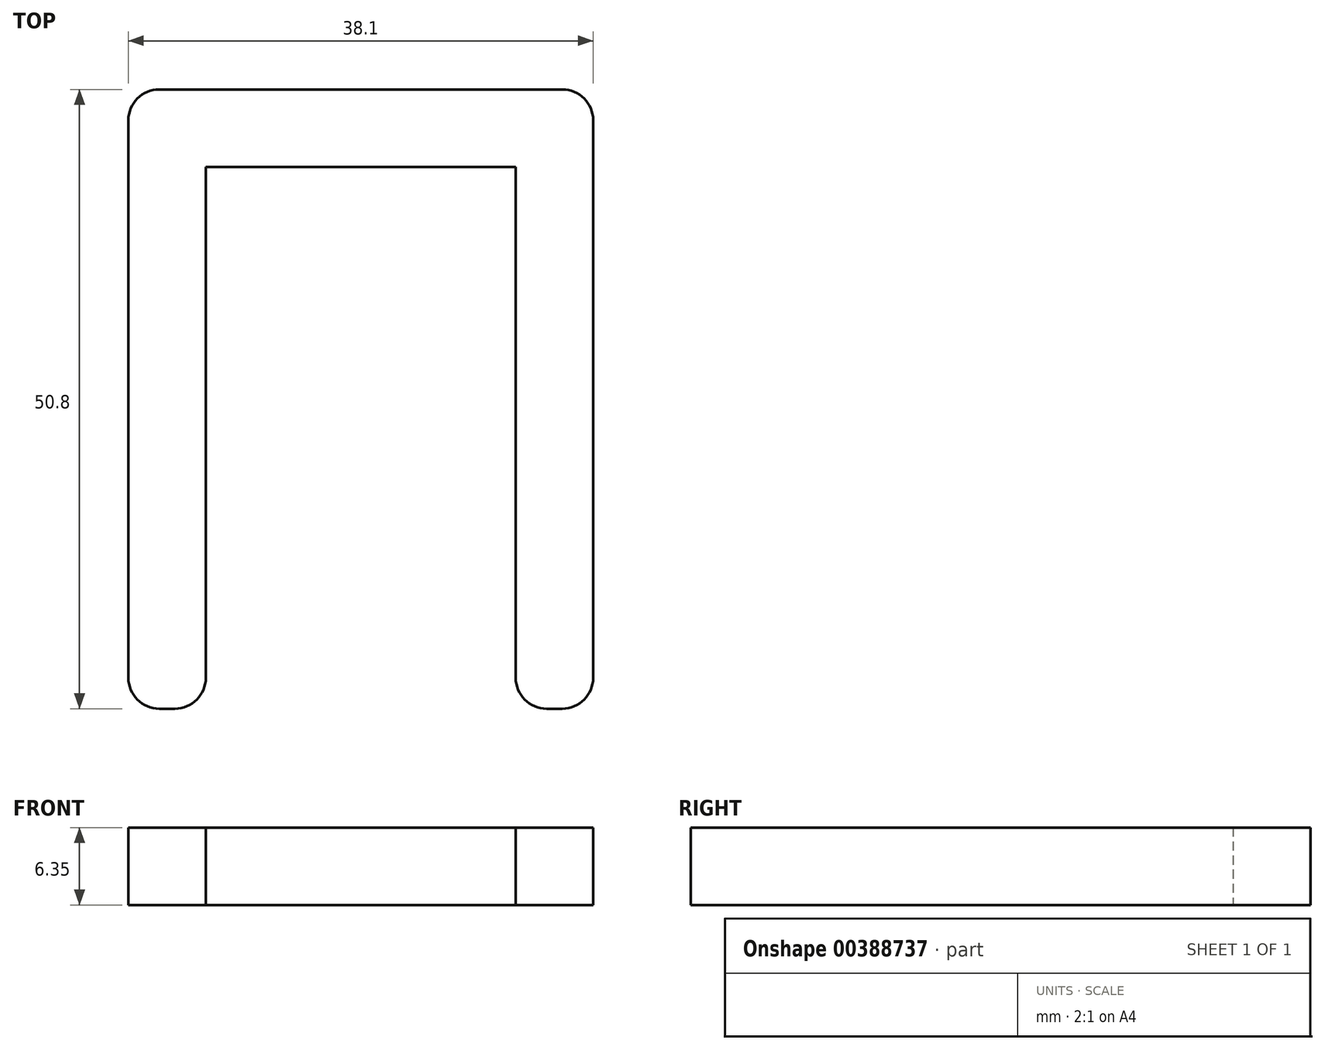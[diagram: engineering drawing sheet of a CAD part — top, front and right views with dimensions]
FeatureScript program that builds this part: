
annotation { "Feature Type Name" : "Feature", "Feature Type Description" : "" }
export const myFeature = defineFeature(function(context is Context, id is Id, definition is map)
    precondition{}
    {
        {
            var Q0;
            Q0=qCreatedBy(makeId("Top.planeOp"),FACE);
            var sketch = newSketch(context, id + "F0", { "sketchPlane" : qUnion([Q0])});
            skLineSegment(sketch, "E0", {"start": v(-20.41, 24.58) * mm, "end": v(4.99, 24.58) * mm});
            skLineSegment(sketch, "E1", {"start": v(4.99, 24.58) * mm, "end": v(4.99, -17.33) * mm});
            skLineSegment(sketch, "E2", {"start": v(-20.41, 24.58) * mm, "end": v(-20.41, -17.33) * mm});
            skLineSegment(sketch, "E3", {"start": v(-22.95, -19.87) * mm, "end": v(-24.22, -19.87) * mm});
            skLineSegment(sketch, "E4", {"start": v(-26.76, -17.33) * mm, "end": v(-26.76, 28.39) * mm});
            skLineSegment(sketch, "E5", {"start": v(7.53, -19.87) * mm, "end": v(8.8, -19.87) * mm});
            skLineSegment(sketch, "E6", {"start": v(11.34, -17.33) * mm, "end": v(11.34, 28.39) * mm});
            skLineSegment(sketch, "E7", {"start": v(-24.22, 30.93) * mm, "end": v(8.8, 30.93) * mm});
            skPoint(sketch, "E8.visualSharp", {"position": v(-26.76, -19.87) * mm});
            skArc(sketch, "E8.filletArc", {"start": v(-26.76, -17.33) * mm, "mid": v(-26.02, -19.13) * mm, "end": v(-24.22, -19.87) * mm});
            skPoint(sketch, "E9.visualSharp", {"position": v(-20.41, -19.87) * mm});
            skArc(sketch, "E9.filletArc", {"start": v(-22.95, -19.87) * mm, "mid": v(-21.15, -19.13) * mm, "end": v(-20.41, -17.33) * mm});
            skPoint(sketch, "E10.visualSharp", {"position": v(4.99, -19.87) * mm});
            skArc(sketch, "E10.filletArc", {"start": v(4.99, -17.33) * mm, "mid": v(5.73, -19.13) * mm, "end": v(7.53, -19.87) * mm});
            skPoint(sketch, "E11.visualSharp", {"position": v(11.34, -19.87) * mm});
            skArc(sketch, "E11.filletArc", {"start": v(8.8, -19.87) * mm, "mid": v(10.6, -19.13) * mm, "end": v(11.34, -17.33) * mm});
            skPoint(sketch, "E12.visualSharp", {"position": v(-26.76, 30.93) * mm});
            skArc(sketch, "E12.filletArc", {"start": v(-24.22, 30.93) * mm, "mid": v(-26.02, 30.19) * mm, "end": v(-26.76, 28.39) * mm});
            skPoint(sketch, "E13.visualSharp", {"position": v(11.34, 30.93) * mm});
            skArc(sketch, "E13.filletArc", {"start": v(11.34, 28.39) * mm, "mid": v(10.6, 30.19) * mm, "end": v(8.8, 30.93) * mm});
            skSolve(sketch);
        }
        {
            var Q0;
            Q0=makeQuery(id+"F0.imprint","IMPRINT",FACE,{"disambiguationData":[TD([[makeQuery(id+"F0.imprint","IMPRINT",EDGE,{"derivedFrom":sQuery(id+"F0.wireOp",EDGE,"E0")}),1.0]])]});
            extrude(context, id + "F1", {"entities" : qUnion([Q0]), "depth" : 6.35 * mm});
        }
    });
